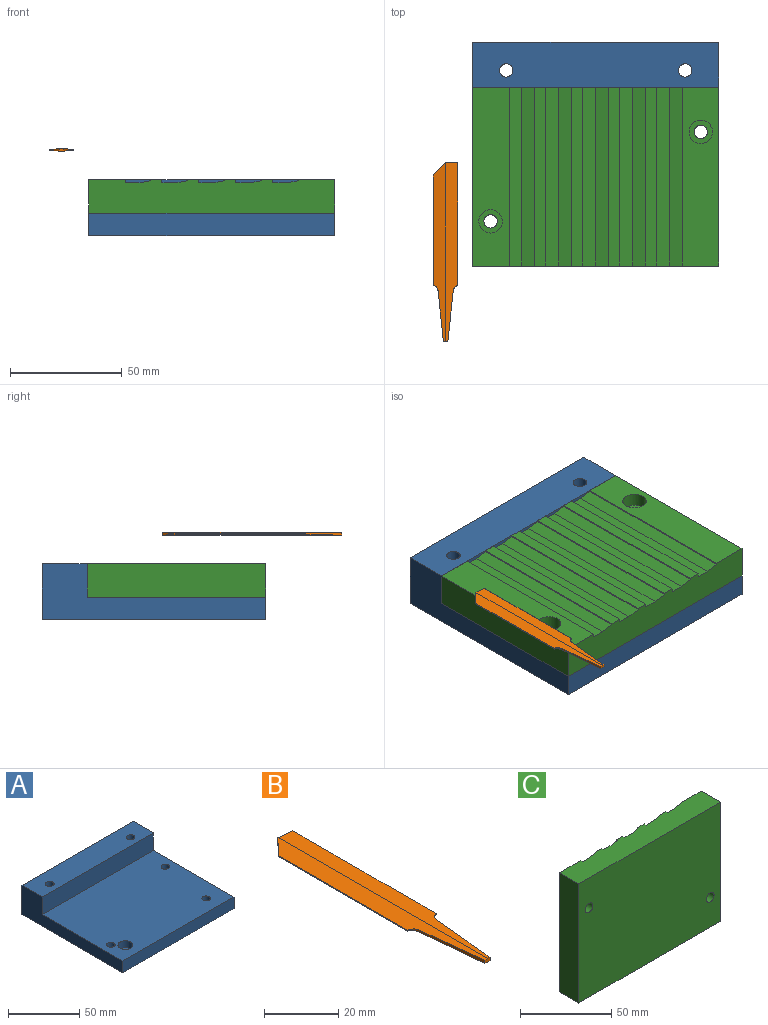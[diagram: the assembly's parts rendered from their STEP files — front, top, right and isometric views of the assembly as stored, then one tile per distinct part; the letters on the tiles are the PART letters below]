
ASSEMBLY  parts=3 mates=1
PART A: 16 faces, bbox 110x100x25 mm
  f0: cylinder r=3mm len=6mm, axis (0,0,-1), area 75.4mm2, adj f9,f12
  f1: plane 100x25mm, normal (1,0,0), area 1300mm2, adj f2,f4,f5,f9,f10,f11
  f2: plane 110x10mm, normal (0,-1,0), area 1100mm2, adj f1,f6,f9,f11
  f3: cylinder r=3mm len=10mm, axis (0,0,-1), area 188.5mm2, adj f9,f11
  f4: plane 110x20mm, normal (0,0,1), area 2143.5mm2, adj f1,f5,f6,f7,f8,f10
  f5: plane 110x25mm, normal (0,1,0), area 2750mm2, adj f1,f4,f6,f9
  f6: plane 100x25mm, normal (-1,0,0), area 1300mm2, adj f2,f4,f5,f9,f10,f11
  f7: cylinder r=3mm len=25mm, axis (0,0,-1), area 471.2mm2, adj f4,f9
  f8: cylinder r=3mm len=25mm, axis (0,0,-1), area 471.2mm2, adj f4,f9
  f9: plane 110x100mm, normal (0,0,-1), area 10830.4mm2, adj f0,f1,f2,f3,f5,f6,f7,f8
  f10: plane 110x15mm, normal (0,-1,0), area 1650mm2, adj f1,f4,f6,f11
  f11: plane 110x80mm, normal (0,0,1), area 8628.6mm2, adj f1,f2,f3,f6,f10,f13,f14,f15
  f12: plane 10.5x10.5mm, normal (0,0,1), area 58.3mm2, adj f0,f13
  f13: cylinder r=5.25mm len=10.5mm, axis (0,0,1), area 197.9mm2, adj f11,f12
  f14: cylinder r=3mm len=10mm, axis (0,0,1), area 188.5mm2, adj f9,f11
  f15: cylinder r=3mm len=10mm, axis (0,0,1), area 188.5mm2, adj f9,f11
PART B: 13 faces, bbox 11x80x1.2 mm
  f0: plane 49.5x0.3mm, normal (-1,0,0), area 14.8mm2, adj f1,f2,f6,f12
  f1: plane 80x5.5mm, normal (-0.09,0,-1), area 347.5mm2, adj f0,f3,f5,f6,f10,f12
  f2: plane 80x5.5mm, normal (-0.09,0,1), area 347.5mm2, adj f0,f3,f5,f6,f11,f12
  f3: plane 2x1.24mm, normal (0,-1,0), area 2.3mm2, adj f1,f2,f5,f8,f10,f11
  f4: plane 5.5x1.24mm, normal (0,1,0), area 4.2mm2, adj f7,f10,f11,f12
  f5: plane 22.79x2.4mm, normal (-0.99,-0.1,0), area 19.8mm2, adj f1,f2,f3,f6
  f6: cylinder r=2.5mm len=2.21mm, axis (0,0,-1), area 1.7mm2, adj f0,f1,f2,f5
  f7: plane 55x0.3mm, normal (1,0,0), area 16.5mm2, adj f4,f9,f10,f11
  f8: plane 22.79x2.4mm, normal (0.99,-0.1,0), area 19.8mm2, adj f3,f9,f10,f11
  f9: cylinder r=2.5mm len=2.21mm, axis (0,0,1), area 1.7mm2, adj f7,f8,f10,f11
  f10: plane 80x5.5mm, normal (0.09,0,-1), area 362.6mm2, adj f1,f3,f4,f7,f8,f9
  f11: plane 80x5.5mm, normal (0.09,0,1), area 362.6mm2, adj f2,f3,f4,f7,f8,f9
  f12: plane 5.5x5.5mm, normal (-0.71,0.71,0), area 6mm2, adj f0,f1,f2,f4
PART C: 41 faces, bbox 110x15x80 mm
  f0: cylinder r=3mm len=9mm, axis (0,1,0), area 169.6mm2, adj f12,f39
  f1: cylinder r=3mm len=9mm, axis (0,1,0), area 169.6mm2, adj f12,f37
  f2: plane 110x15mm, normal (0,0,-1), area 1539.1mm2, adj f3,f4,f5,f6,f7,f9,f10,f11
  f3: plane 80x16.25mm, normal (0,1,0), area 1213.4mm2, adj f2,f8,f11,f31,f38
  f4: plane 80x5mm, normal (0,1,0), area 400mm2, adj f2,f8,f27,f30
  f5: plane 80x5mm, normal (0,1,0), area 400mm2, adj f2,f8,f23,f26
  f6: plane 80x5mm, normal (0,1,0), area 400mm2, adj f2,f8,f17,f22
  f7: plane 80x5mm, normal (0,1,0), area 400mm2, adj f2,f8,f13,f20
  f8: plane 110x15mm, normal (0,0,1), area 1578.3mm2, adj f3,f4,f5,f6,f7,f9,f10,f11
  f9: plane 80x15mm, normal (1,0,0), area 1200mm2, adj f2,f8,f10,f12
  f10: plane 80x16.25mm, normal (0,1,0), area 1213.4mm2, adj f2,f8,f9,f16,f40
  f11: plane 80x15mm, normal (-1,0,0), area 1200mm2, adj f2,f3,f8,f12
  f12: plane 110x80mm, normal (0,-1,0), area 8743.5mm2, adj f0,f1,f2,f8,f9,f11
  f13: plane 80x1.5mm, normal (1,0,0), area 120mm2, adj f2,f7,f8,f14
  f14: plane 80x5.75mm, normal (0,1,0), area 460mm2, adj f2,f8,f13,f15
  f15: plane 80x5.75mm, normal (-0.17,0.98,0), area 467.1mm2, adj f2,f8,f14,f16
  f16: plane 80x0.49mm, normal (-1,0,0), area 38.9mm2, adj f2,f8,f10,f15
  f17: plane 80x1.5mm, normal (1,0,0), area 120mm2, adj f2,f6,f8,f18
  f18: plane 80x5.75mm, normal (0,1,0), area 460mm2, adj f2,f8,f17,f19
  f19: plane 80x5.75mm, normal (-0.17,0.98,0), area 467.1mm2, adj f2,f8,f18,f20
  f20: plane 80x0.49mm, normal (-1,0,0), area 38.9mm2, adj f2,f7,f8,f19
  f21: plane 80x5.75mm, normal (-0.17,0.98,0), area 467.1mm2, adj f2,f8,f22,f24
  f22: plane 80x0.49mm, normal (-1,0,0), area 38.9mm2, adj f2,f6,f8,f21
  f23: plane 80x1.5mm, normal (1,0,0), area 120mm2, adj f2,f5,f8,f24
  f24: plane 80x5.75mm, normal (0,1,0), area 460mm2, adj f2,f8,f21,f23
  f25: plane 80x5.75mm, normal (-0.17,0.98,0), area 467.1mm2, adj f2,f8,f26,f28
  f26: plane 80x0.49mm, normal (-1,0,0), area 38.9mm2, adj f2,f5,f8,f25
  f27: plane 80x1.5mm, normal (1,0,0), area 120mm2, adj f2,f4,f8,f28
  f28: plane 80x5.75mm, normal (0,1,0), area 460mm2, adj f2,f8,f25,f27
  f29: plane 80x5.75mm, normal (-0.17,0.98,0), area 467.1mm2, adj f2,f8,f30,f32
  f30: plane 80x0.49mm, normal (-1,0,0), area 38.9mm2, adj f2,f4,f8,f29
  f31: plane 80x1.5mm, normal (1,0,0), area 120mm2, adj f2,f3,f8,f32
  f32: plane 80x5.75mm, normal (0,1,0), area 460mm2, adj f2,f8,f29,f31
  f33: cylinder r=2.5mm len=15mm, axis (0,0,-1), area 235.1mm2, adj f2,f34,f39,f40
  f34: plane 5x5mm, normal (0,0,-1), area 17.8mm2, adj f33,f39,f40
  f35: cylinder r=2.5mm len=15mm, axis (0,0,-1), area 235.6mm2, adj f2,f36
  f36: plane 5x5mm, normal (0,0,-1), area 19.6mm2, adj f35
  f37: plane 10.5x10.5mm, normal (0,1,0), area 58.3mm2, adj f1,f38
  f38: cylinder r=5.25mm len=10.5mm, axis (0,1,0), area 197.9mm2, adj f3,f37
  f39: plane 10.5x10.49mm, normal (0,1,0), area 58mm2, adj f0,f33,f34,f40
  f40: cylinder r=5.25mm len=10.5mm, axis (0,1,0), area 196mm2, adj f10,f33,f34,f39
PLACE A t=(-50.48,-28.54,-11.6)mm
PLACE B t=(-117.58,-72.35,26.08)mm
PLACE C rot(axis=(1,0,0),90deg) t=(-50.48,1.46,5.9)mm
MATE fastened C.f1 <-> A.f15  axis (0,0,-1) through (-97.48,-58.54,-1.6)mm
